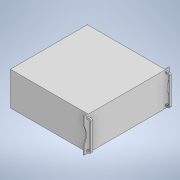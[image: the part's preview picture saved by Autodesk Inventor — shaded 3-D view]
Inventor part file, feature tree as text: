
AUTODESK INVENTOR PART (.ipt)
format: ipt  version: 2022 (Build 260153000, 153)  size: 207,360 bytes
history: native  units: in
note: dims shown in document units (in); Inventor stores cm internally (conversion verified against a paired STEP export)
features: fillet x8, extrude x7, sketch x7, mirror x3
ambient origin geometry x8: Origin, YZ Plane, XZ Plane, XY Plane, X Axis, Y Axis, Z Axis, Center Point
bodies: Solid1 (feature_tree)
feature tree (25):
  extrude  "Extrusion1"  Depth=18.1102in
  extrude  "Extrusion3"  Depth=0.1969in
  extrude  "Extrusion4"  Depth=0.1969in
  extrude  "Extrusion5"  Depth=0.9843in
  extrude  "Extrusion6"  TaperAngle=90.0deg  [1 undecoded]
  mirror  "Mirror1"
  extrude  "Extrusion7"  Depth=3.937in
  mirror  "Mirror2"
  extrude  "Extrusion8"  Depth=0.9843in TaperAngle=0.0deg
  mirror  "Mirror3"
  fillet  "Face Fillet1"
  fillet  "Face Fillet2"
  fillet  "Face Fillet3"
  fillet  "Face Fillet4"
  fillet  "Face Fillet5"
  fillet  "Face Fillet6"
  fillet  "Face Fillet7"
  fillet  "Face Fillet8"
  sketch  "Sketch1"  dims[d0=18.3071in d1=18.1102in]
  sketch  "Sketch3"  dims[d2=7.874in d3=0.0in d6=0.1969in]
  sketch  "Sketch4"  dims[d7=0.9843in d8=0.0in d10=0.1969in]
  sketch  "Sketch5"  dims[d11=0.9843in d12=0.0in d13=1.9685in]
  sketch  "Sketch6"  dims[d14=1.9685in d15=90.0deg]
  sketch  "Sketch7"  dims[d16=3.937in d17=1.9685in]
  sketch  "Sketch8"  dims[d18=3.937in d19=0.9843in d20=0.0in d22=0.3937in d23=0.3937in d24=0.9843in d25=0.0in d27=0.3937in d28=0.3937in d29=0.9843in d30=0.0in d31=0.1969in d32=90.0deg d33=6.2992in d34=0.0in d35=0.3937in d36=0.3937in d37=0.3937in d38=0.3937in d39=0.3937in d40=0.3937in d41=0.3937in d42=0.3937in]
note: 1 required parameter value undecoded (feature->parameter linkage not recoverable at this tier; creation-order binding heuristic only, values carry confidence <= 0.55)
